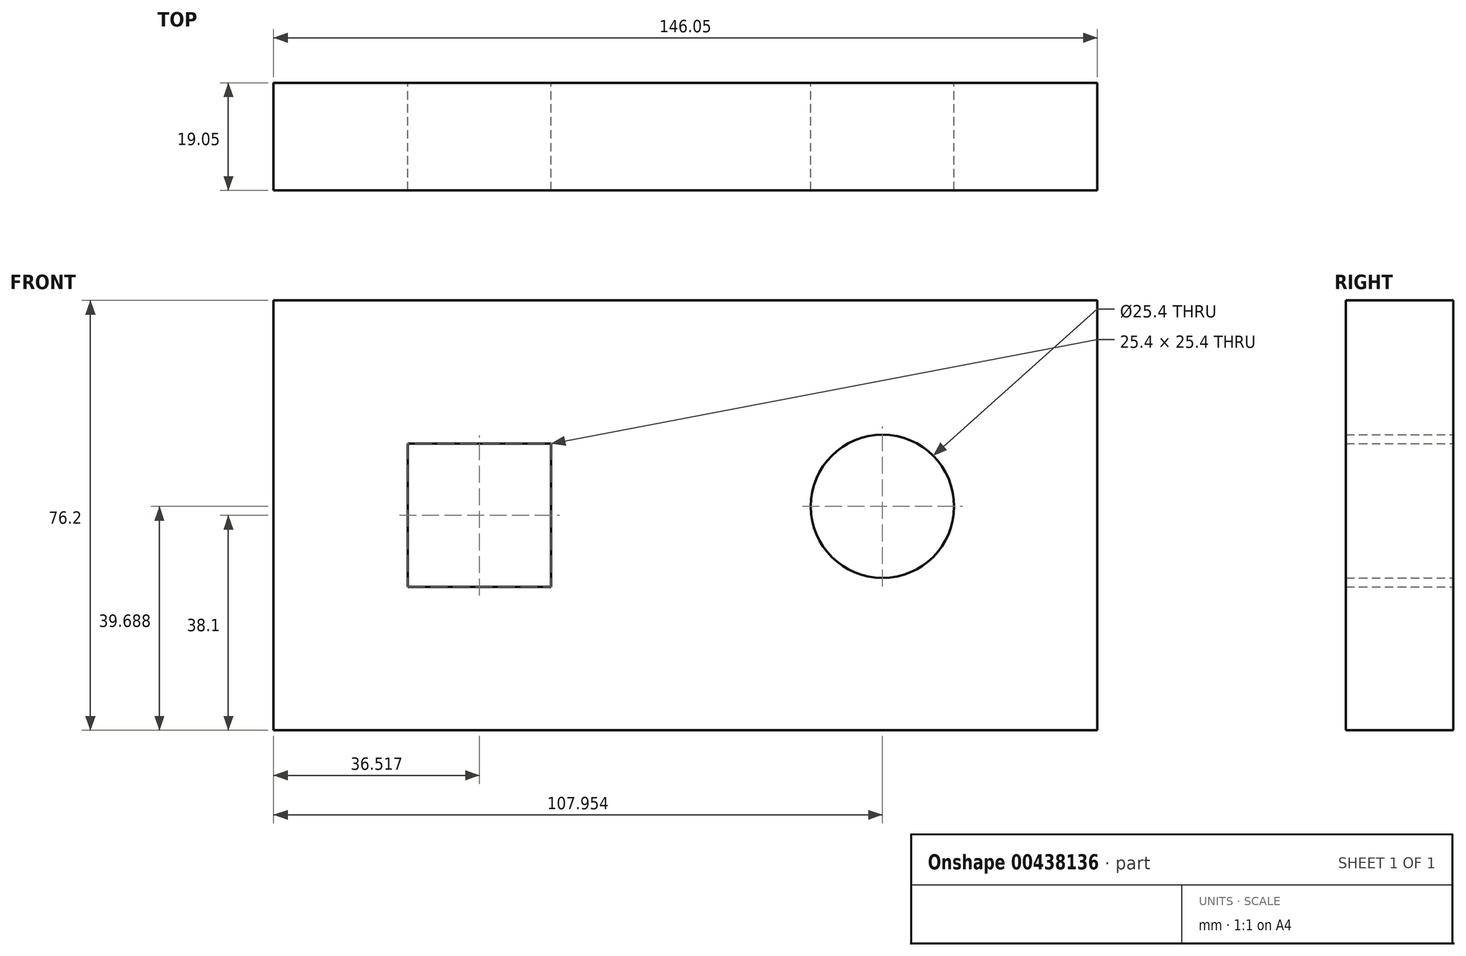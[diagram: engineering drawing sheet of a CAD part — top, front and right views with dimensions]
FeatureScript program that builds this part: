
annotation { "Feature Type Name" : "Feature", "Feature Type Description" : "" }
export const myFeature = defineFeature(function(context is Context, id is Id, definition is map)
    precondition{}
    {
        {
            var Q0;
            Q0=qCreatedBy(makeId("Front.planeOp"),FACE);
            var sketch = newSketch(context, id + "F0", { "sketchPlane" : qUnion([Q0])});
            skLineSegment(sketch, "E0.bottom", {"start": v(-73.14, 76.2) * mm, "end": v(72.91, 76.2) * mm});
            skLineSegment(sketch, "E0.top", {"start": v(-73.14, 0) * mm, "end": v(72.91, 0) * mm});
            skLineSegment(sketch, "E0.left", {"start": v(-73.14, 76.2) * mm, "end": v(-73.14, 0) * mm});
            skLineSegment(sketch, "E0.right", {"start": v(72.91, 76.2) * mm, "end": v(72.91, 0) * mm});
            skCircle(sketch, "E1", {"center": v(34.81, 39.69) * mm, "radius": 12.7 * mm});
            skLineSegment(sketch, "E2.bottom", {"start": v(-49.32, 50.8) * mm, "end": v(-23.92, 50.8) * mm});
            skLineSegment(sketch, "E2.top", {"start": v(-49.32, 25.4) * mm, "end": v(-23.92, 25.4) * mm});
            skLineSegment(sketch, "E2.left", {"start": v(-49.32, 50.8) * mm, "end": v(-49.32, 25.4) * mm});
            skLineSegment(sketch, "E2.right", {"start": v(-23.92, 50.8) * mm, "end": v(-23.92, 25.4) * mm});
            skSolve(sketch);
        }
        {
            var Q0;
            Q0=makeQuery(id+"F0.imprint","IMPRINT",FACE,{"disambiguationData":[TD([[makeQuery(id+"F0.imprint","IMPRINT",EDGE,{"derivedFrom":sQuery(id+"F0.wireOp",EDGE,"E0.bottom")}),-1.0]])]});
            extrude(context, id + "F1", {"entities" : qUnion([Q0]), "depth" : 19.05 * mm});
        }
    });
